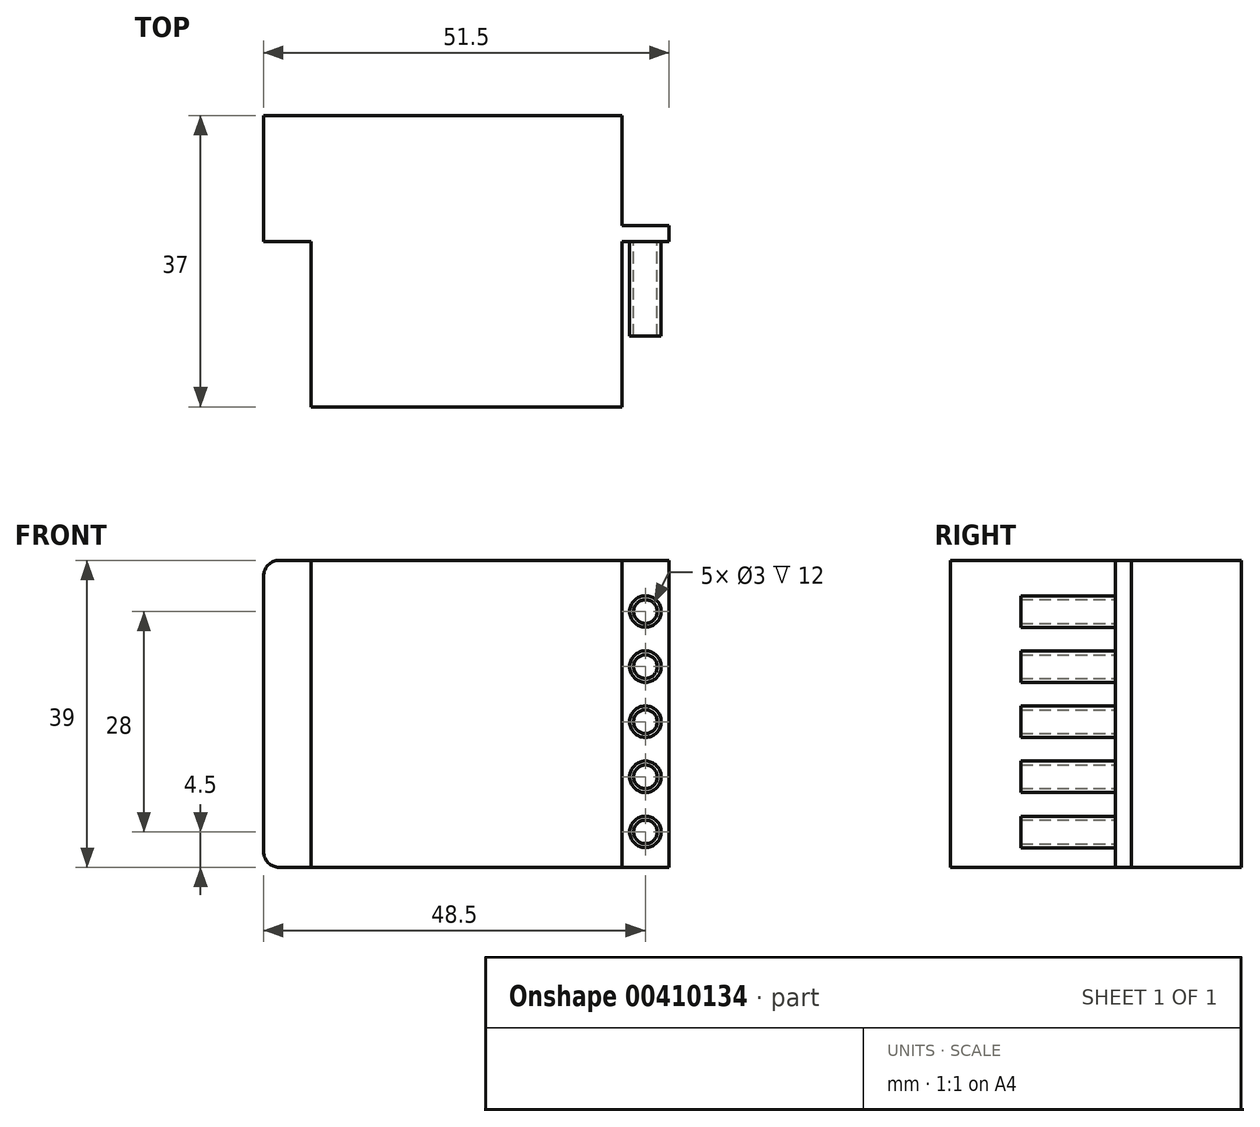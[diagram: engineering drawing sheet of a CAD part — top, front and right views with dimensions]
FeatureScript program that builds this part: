
annotation { "Feature Type Name" : "Feature", "Feature Type Description" : "" }
export const myFeature = defineFeature(function(context is Context, id is Id, definition is map)
    precondition{}
    {
        {
            var Q0;
            Q0=qCreatedBy(makeId("Top.planeOp"),FACE);
            var sketch = newSketch(context, id + "F0", { "sketchPlane" : qUnion([Q0])});
            skLineSegment(sketch, "E0.bottom", {"start": v(0, 0) * mm, "end": v(51.5, 0) * mm});
            skLineSegment(sketch, "E0.top", {"start": v(0, 37) * mm, "end": v(51.5, 37) * mm});
            skLineSegment(sketch, "E0.left", {"start": v(0, 0) * mm, "end": v(0, 37) * mm});
            skLineSegment(sketch, "E0.right", {"start": v(51.5, 0) * mm, "end": v(51.5, 37) * mm});
            skSolve(sketch);
        }
        {
            var Q0;
            Q0=qSketchRegion(id+"F0",true);
            extrude(context, id + "F1", {"entities" : qUnion([Q0]), "depth" : 39 * mm});
        }
        {
            var Q0;
            Q0=makeQuery(id+"F1.opExtrude","CAP_FACE",FACE,{"disambiguationData":[OSD([sQuery(id+"F0.wireOp",EDGE,"E0.bottom"),sQuery(id+"F0.wireOp",EDGE,"E0.top"),sQuery(id+"F0.wireOp",EDGE,"E0.left"),sQuery(id+"F0.wireOp",EDGE,"E0.right")])],"isStart":true});
            var sketch = newSketch(context, id + "F2", { "sketchPlane" : qUnion([Q0])});
            skLineSegment(sketch, "E1.bottom", {"start": v(0, 0) * mm, "end": v(6, 0) * mm});
            skLineSegment(sketch, "E1.top", {"start": v(0, -21) * mm, "end": v(6, -21) * mm});
            skLineSegment(sketch, "E1.left", {"start": v(0, 0) * mm, "end": v(0, -21) * mm});
            skLineSegment(sketch, "E1.right", {"start": v(6, 0) * mm, "end": v(6, -21) * mm});
            skLineSegment(sketch, "E2.bottom", {"start": v(51.5, 0) * mm, "end": v(45.5, 0) * mm});
            skLineSegment(sketch, "E2.top", {"start": v(51.5, -21) * mm, "end": v(45.5, -21) * mm});
            skLineSegment(sketch, "E2.left", {"start": v(51.5, 0) * mm, "end": v(51.5, -21) * mm});
            skLineSegment(sketch, "E2.right", {"start": v(45.5, 0) * mm, "end": v(45.5, -21) * mm});
            skLineSegment(sketch, "E3.bottom", {"start": v(51.5, -37) * mm, "end": v(45.5, -37) * mm});
            skLineSegment(sketch, "E3.top", {"start": v(51.5, -23) * mm, "end": v(45.5, -23) * mm});
            skLineSegment(sketch, "E3.left", {"start": v(51.5, -37) * mm, "end": v(51.5, -23) * mm});
            skLineSegment(sketch, "E3.right", {"start": v(45.5, -37) * mm, "end": v(45.5, -23) * mm});
            skSolve(sketch);
        }
        {
            var Q0;
            Q0 = qSketchRegion(id + "F2", true);
            extrude(context, id + "F3", {"entities" : qUnion([Q0]), "operationType" : NewBodyOperationType.REMOVE, "endBound" : BoundingType.THROUGH_ALL, "oppositeDirection" : true, "depth" : 25 * mm});
        }
        {
            var Q0;
            Q0=makeQuery(id+"F3.boolean.opBoolean","COPY",FACE,{"derivedFrom":makeQuery(id+"F3.opExtrude","SWEPT_FACE",FACE,{"disambiguationData":[OSD([sQuery(id+"F2.wireOp",EDGE,"E2.top")])]})});
            var sketch = newSketch(context, id + "F4", { "sketchPlane" : qUnion([Q0])});
            skLineSegment(sketch, "E4", {"start": v(48.5, 39) * mm, "end": v(48.5, 0) * mm, "construction": true});
            skCircle(sketch, "E5", {"center": v(48.5, 4.5) * mm, "radius": 2 * mm});
            skCircle(sketch, "E6", {"center": v(48.5, 4.5) * mm, "radius": 1.5 * mm});
            skCircle(sketch, "E7.0.1.0", {"center": v(48.5, 11.5) * mm, "radius": 1.5 * mm});
            skCircle(sketch, "E7.0.1.1", {"center": v(48.5, 11.5) * mm, "radius": 2 * mm});
            skCircle(sketch, "E7.0.2.0", {"center": v(48.5, 18.5) * mm, "radius": 1.5 * mm});
            skCircle(sketch, "E7.0.2.1", {"center": v(48.5, 18.5) * mm, "radius": 2 * mm});
            skCircle(sketch, "E7.0.3.0", {"center": v(48.5, 25.5) * mm, "radius": 1.5 * mm});
            skCircle(sketch, "E7.0.3.1", {"center": v(48.5, 25.5) * mm, "radius": 2 * mm});
            skCircle(sketch, "E7.0.4.0", {"center": v(48.5, 32.5) * mm, "radius": 1.5 * mm});
            skCircle(sketch, "E7.0.4.1", {"center": v(48.5, 32.5) * mm, "radius": 2 * mm});
            skLineSegment(sketch, "E7.direction1", {"start": v(48.5, 4.5) * mm, "end": v(73.5, 4.5) * mm, "construction": true});
            skLineSegment(sketch, "E7.direction2", {"start": v(48.5, 4.5) * mm, "end": v(48.5, 11.5) * mm, "construction": true});
            skSolve(sketch);
        }
        {
            var Q0;
            Q0 = qSketchRegion(id + "F4", true);
            extrude(context, id + "F5", {"entities" : qUnion([Q0]), "operationType" : NewBodyOperationType.ADD, "depth" : 12 * mm});
        }
        {
            var Q0;
            Q0=makeQuery(id+"F1.opExtrude","CAP_EDGE",EDGE,{"disambiguationData":[OSD([sQuery(id+"F0.wireOp",EDGE,"E0.left")])],"isStart":true});
            var Q1;
            Q1=makeQuery(id+"F1.opExtrude","CAP_EDGE",EDGE,{"disambiguationData":[OSD([sQuery(id+"F0.wireOp",EDGE,"E0.left")])],"isStart":false});
            fillet(context, id + "F6", {"entities" : qUnion([Q0, Q1]), "radius" : 2 * mm, "tangentPropagation" : true, "allowEdgeOverflow" : false});
        }
    });
